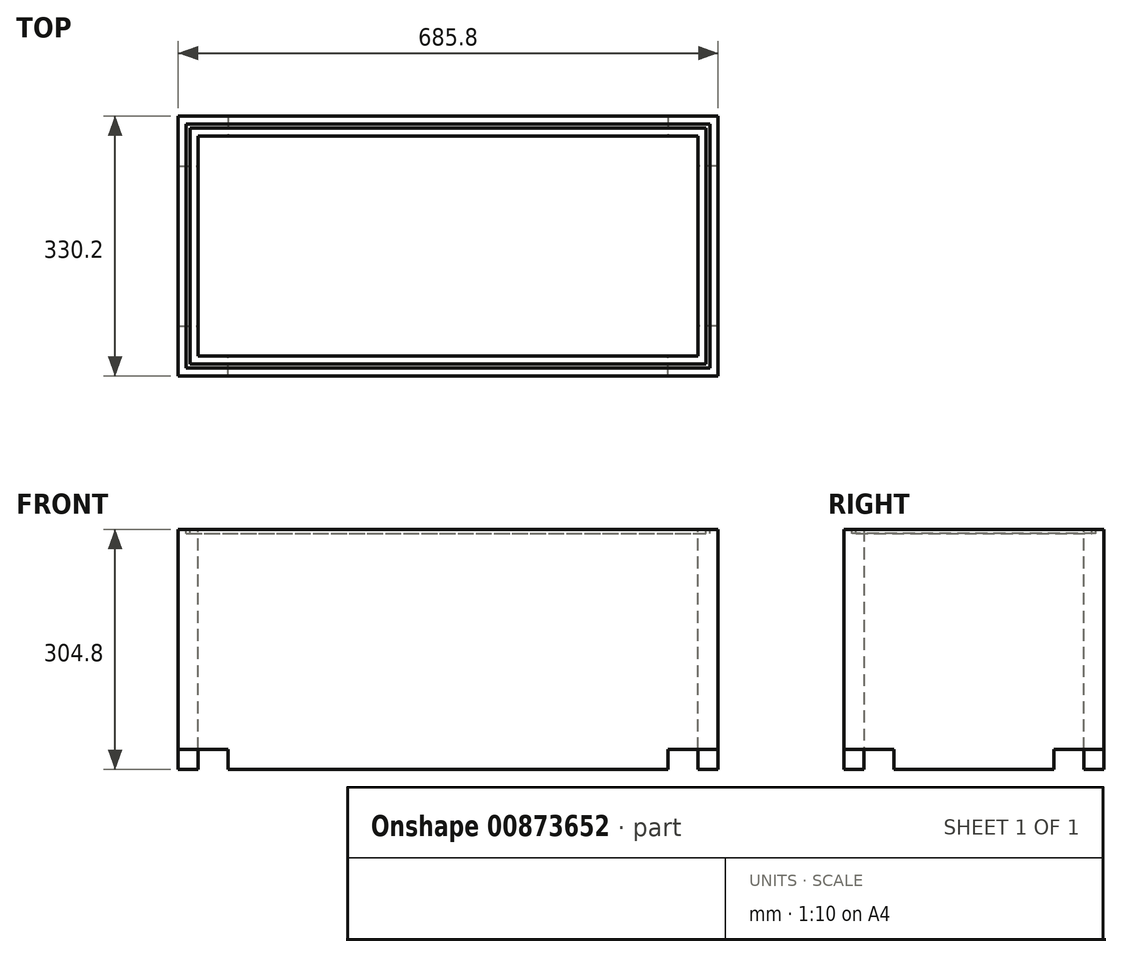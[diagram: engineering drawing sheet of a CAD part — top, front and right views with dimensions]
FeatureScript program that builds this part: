
annotation { "Feature Type Name" : "Feature", "Feature Type Description" : "" }
export const myFeature = defineFeature(function(context is Context, id is Id, definition is map)
    precondition{}
    {
        {
            var Q0;
            Q0=qCreatedBy(makeId("Top.planeOp"),FACE);
            var sketch = newSketch(context, id + "F0", { "sketchPlane" : qUnion([Q0])});
            skLineSegment(sketch, "E0.bottom", {"start": v(0, 0) * mm, "end": v(685.8, 0) * mm});
            skLineSegment(sketch, "E0.top", {"start": v(0, -25.4) * mm, "end": v(685.8, -25.4) * mm});
            skLineSegment(sketch, "E0.left", {"start": v(0, 0) * mm, "end": v(0, -25.4) * mm});
            skLineSegment(sketch, "E0.right", {"start": v(685.8, 0) * mm, "end": v(685.8, -25.4) * mm});
            skSolve(sketch);
        }
        {
            var Q0;
            Q0 = qSketchRegion(id + "F0", true);
            extrude(context, id + "F1", {"entities" : qUnion([Q0]), "depth" : 304.8 * mm, "offsetDistance" : 25.4 * mm});
        }
        {
            var Q0;
            Q0=makeQuery(id+"F1.opExtrude","SWEPT_FACE",FACE,{"disambiguationData":[OSD([sQuery(id+"F0.wireOp",EDGE,"E0.top")])]});
            var sketch = newSketch(context, id + "F2", { "sketchPlane" : qUnion([Q0])});
            skLineSegment(sketch, "E1.bottom", {"start": v(685.8, 0) * mm, "end": v(660.4, 0) * mm});
            skLineSegment(sketch, "E1.top", {"start": v(685.8, 304.8) * mm, "end": v(660.4, 304.8) * mm});
            skLineSegment(sketch, "E1.left", {"start": v(685.8, 0) * mm, "end": v(685.8, 304.8) * mm});
            skLineSegment(sketch, "E1.right", {"start": v(660.4, 0) * mm, "end": v(660.4, 304.8) * mm});
            skLineSegment(sketch, "E2.bottom", {"start": v(0, 0) * mm, "end": v(25.4, 0) * mm});
            skLineSegment(sketch, "E2.top", {"start": v(0, 304.8) * mm, "end": v(25.4, 304.8) * mm});
            skLineSegment(sketch, "E2.left", {"start": v(0, 0) * mm, "end": v(0, 304.8) * mm});
            skLineSegment(sketch, "E2.right", {"start": v(25.4, 0) * mm, "end": v(25.4, 304.8) * mm});
            skSolve(sketch);
        }
        {
            var Q0;
            Q0=makeQuery(id+"F2.imprint","IMPRINT",FACE,{"disambiguationData":[TD([[makeQuery(id+"F2.imprint","IMPRINT",EDGE,{"derivedFrom":sQuery(id+"F2.wireOp",EDGE,"E1.bottom")}),1.0]])]});
            extrude(context, id + "F3", {"entities" : qUnion([Q0]), "operationType" : NewBodyOperationType.ADD, "depth" : 304.8 * mm, "offsetDistance" : 25.4 * mm});
        }
        {
            var Q0;
            Q0=makeQuery(id+"F2.imprint","IMPRINT",FACE,{"disambiguationData":[TD([[makeQuery(id+"F2.imprint","IMPRINT",EDGE,{"derivedFrom":sQuery(id+"F2.wireOp",EDGE,"E2.bottom")}),1.0]])]});
            extrude(context, id + "F4", {"entities" : qUnion([Q0]), "operationType" : NewBodyOperationType.ADD, "depth" : 304.8 * mm, "offsetDistance" : 25.4 * mm});
        }
        {
            var Q0;
            Q0=makeQuery(id+"F4.opExtrude","SWEPT_FACE",FACE,{"disambiguationData":[OSD([sQuery(id+"F2.wireOp",EDGE,"E2.right")])]});
            var sketch = newSketch(context, id + "F5", { "sketchPlane" : qUnion([Q0])});
            skLineSegment(sketch, "E3.bottom", {"start": v(-330.2, 304.8) * mm, "end": v(-304.8, 304.8) * mm});
            skLineSegment(sketch, "E3.top", {"start": v(-330.2, 0) * mm, "end": v(-304.8, 0) * mm});
            skLineSegment(sketch, "E3.left", {"start": v(-330.2, 304.8) * mm, "end": v(-330.2, 0) * mm});
            skLineSegment(sketch, "E3.right", {"start": v(-304.8, 304.8) * mm, "end": v(-304.8, 0) * mm});
            skSolve(sketch);
        }
        {
            var Q0;
            Q0=makeQuery(id+"F5.imprint","IMPRINT",FACE,{"disambiguationData":[TD([[makeQuery(id+"F5.imprint","IMPRINT",EDGE,{"derivedFrom":sQuery(id+"F5.wireOp",EDGE,"E3.bottom")}),-1.0]])]});
            extrude(context, id + "F6", {"entities" : qUnion([Q0]), "operationType" : NewBodyOperationType.ADD, "depth" : 660.4 * mm, "offsetDistance" : 25.4 * mm});
        }
        {
            var Q0;
            Q0=makeQuery(id+"F6.boolean.opBoolean","MERGE",FACE,{"derivedFrom":[makeQuery(id+"F4.boolean.opBoolean","MERGE",FACE,{"derivedFrom":[makeQuery(id+"F3.boolean.opBoolean","MERGE",FACE,{"derivedFrom":[makeQuery(id+"F1.opExtrude","CAP_FACE",FACE,{"disambiguationData":[OSD([sQuery(id+"F0.wireOp",EDGE,"E0.bottom"),sQuery(id+"F0.wireOp",EDGE,"E0.top"),sQuery(id+"F0.wireOp",EDGE,"E0.left"),sQuery(id+"F0.wireOp",EDGE,"E0.right")])],"isStart":false}),makeQuery(id+"F3.opExtrude","SWEPT_FACE",FACE,{"disambiguationData":[OSD([sQuery(id+"F2.wireOp",EDGE,"E1.top")])]})]}),makeQuery(id+"F4.opExtrude","SWEPT_FACE",FACE,{"disambiguationData":[OSD([sQuery(id+"F2.wireOp",EDGE,"E2.top")])]})]}),makeQuery(id+"F6.opExtrude","SWEPT_FACE",FACE,{"disambiguationData":[OSD([sQuery(id+"F5.wireOp",EDGE,"E3.bottom")])]})]});
            var sketch = newSketch(context, id + "F7", { "sketchPlane" : qUnion([Q0])});
            skLineSegment(sketch, "E4.bottom", {"start": v(12.7, -10.16) * mm, "end": v(673.1, -10.16) * mm});
            skLineSegment(sketch, "E4.top", {"start": v(15.24, -15.24) * mm, "end": v(673.1, -15.24) * mm});
            skLineSegment(sketch, "E4.right", {"start": v(673.1, -10.16) * mm, "end": v(673.1, -15.24) * mm});
            skLineSegment(sketch, "E5.bottom", {"start": v(10.16, -10.16) * mm, "end": v(15.24, -10.16) * mm});
            skLineSegment(sketch, "E5.top", {"start": v(10.16, -314.96) * mm, "end": v(15.24, -314.96) * mm});
            skLineSegment(sketch, "E5.left", {"start": v(10.16, -10.16) * mm, "end": v(10.16, -314.96) * mm});
            skLineSegment(sketch, "E5.right", {"start": v(15.24, -10.16) * mm, "end": v(15.24, -314.96) * mm});
            skLineSegment(sketch, "E6.top", {"start": v(10.16, -15.24) * mm, "end": v(15.24, -15.24) * mm});
            skLineSegment(sketch, "E6.left", {"start": v(10.16, -10.16) * mm, "end": v(10.16, -15.24) * mm});
            skLineSegment(sketch, "E6.right", {"start": v(15.24, -10.16) * mm, "end": v(15.24, -15.24) * mm});
            skLineSegment(sketch, "E7.top", {"start": v(10.16, -320.04) * mm, "end": v(15.24, -320.04) * mm});
            skLineSegment(sketch, "E7.left", {"start": v(10.16, -314.96) * mm, "end": v(10.16, -320.04) * mm});
            skLineSegment(sketch, "E7.right", {"start": v(15.24, -314.96) * mm, "end": v(15.24, -320.04) * mm});
            skLineSegment(sketch, "E8.bottom", {"start": v(15.24, -314.96) * mm, "end": v(670.56, -314.96) * mm});
            skLineSegment(sketch, "E8.top", {"start": v(15.24, -320.04) * mm, "end": v(670.56, -320.04) * mm});
            skLineSegment(sketch, "E8.right", {"start": v(670.56, -314.96) * mm, "end": v(670.56, -320.04) * mm});
            skLineSegment(sketch, "E9.bottom", {"start": v(670.56, -314.96) * mm, "end": v(675.64, -314.96) * mm});
            skLineSegment(sketch, "E9.top", {"start": v(670.56, -320.04) * mm, "end": v(675.64, -320.04) * mm});
            skLineSegment(sketch, "E9.right", {"start": v(675.64, -314.96) * mm, "end": v(675.64, -320.04) * mm});
            skLineSegment(sketch, "E10.top", {"start": v(670.56, -10.16) * mm, "end": v(675.64, -10.16) * mm});
            skLineSegment(sketch, "E10.left", {"start": v(670.56, -314.96) * mm, "end": v(670.56, -10.16) * mm});
            skLineSegment(sketch, "E10.right", {"start": v(675.64, -314.96) * mm, "end": v(675.64, -10.16) * mm});
            skSolve(sketch);
        }
        {
            var Q0;
            {var subQ0=sQuery(id+"F7.wireOp",EDGE,"E4.bottom");Q0=makeQuery(id+"F7.imprint","IMPRINT",FACE,{"disambiguationData":[TD([[makeQuery(id+"F7.imprint","IMPRINT",EDGE,{"derivedFrom":subQ0}),-1.0]])]});}
            var Q1;
            Q1=makeQuery(id+"F7.imprint","IMPRINT",FACE,{"disambiguationData":[TD([[makeQuery(id+"F7.imprint","IMPRINT",EDGE,{"derivedFrom":sQuery(id+"F7.wireOp",EDGE,"E6.top")}),1.0]])]});
            var Q2;
            Q2=makeQuery(id+"F7.imprint","IMPRINT",FACE,{"disambiguationData":[TD([[makeQuery(id+"F7.imprint","IMPRINT",EDGE,{"derivedFrom":sQuery(id+"F7.wireOp",EDGE,"E5.left")}),1.0]])]});
            var Q3;
            Q3=makeQuery(id+"F7.imprint","IMPRINT",FACE,{"disambiguationData":[TD([[makeQuery(id+"F7.imprint","IMPRINT",EDGE,{"derivedFrom":sQuery(id+"F7.wireOp",EDGE,"E5.top")}),-1.0]])]});
            var Q4;
            Q4=makeQuery(id+"F7.imprint","IMPRINT",FACE,{"disambiguationData":[TD([[makeQuery(id+"F7.imprint","IMPRINT",EDGE,{"derivedFrom":sQuery(id+"F7.wireOp",EDGE,"E8.bottom")}),-1.0]])]});
            var Q5;
            Q5=makeQuery(id+"F7.imprint","IMPRINT",FACE,{"disambiguationData":[TD([[makeQuery(id+"F7.imprint","IMPRINT",EDGE,{"derivedFrom":sQuery(id+"F7.wireOp",EDGE,"E9.top")}),1.0]])]});
            var Q6;
            {var subQ1=sQuery(id+"F7.wireOp",EDGE,"E4.right");Q6=makeQuery(id+"F7.imprint","IMPRINT",FACE,{"disambiguationData":[TD([[makeQuery(id+"F7.imprint","IMPRINT",EDGE,{"derivedFrom":subQ1}),1.0]])]});}
            var Q7;
            {var subQ0=sQuery(id+"F7.wireOp",EDGE,"E4.right");Q7=makeQuery(id+"F7.imprint","IMPRINT",FACE,{"disambiguationData":[TD([[makeQuery(id+"F7.imprint","IMPRINT",EDGE,{"derivedFrom":subQ0}),-1.0]])]});}
            extrude(context, id + "F8", {"entities" : qUnion([Q0, Q1, Q2, Q3, Q4, Q5, Q6, Q7]), "operationType" : NewBodyOperationType.REMOVE, "oppositeDirection" : true, "depth" : 5.08 * mm, "offsetDistance" : 25.4 * mm});
        }
        {
            var Q0;
            Q0=makeQuery(id+"F6.boolean.opBoolean","MERGE",FACE,{"derivedFrom":[makeQuery(id+"F4.boolean.opBoolean","MERGE",FACE,{"derivedFrom":[makeQuery(id+"F3.boolean.opBoolean","MERGE",FACE,{"derivedFrom":[makeQuery(id+"F1.opExtrude","CAP_FACE",FACE,{"disambiguationData":[OSD([sQuery(id+"F0.wireOp",EDGE,"E0.bottom"),sQuery(id+"F0.wireOp",EDGE,"E0.top"),sQuery(id+"F0.wireOp",EDGE,"E0.left"),sQuery(id+"F0.wireOp",EDGE,"E0.right")])],"isStart":true}),makeQuery(id+"F3.opExtrude","SWEPT_FACE",FACE,{"disambiguationData":[OSD([sQuery(id+"F2.wireOp",EDGE,"E1.bottom")])]})]}),makeQuery(id+"F4.opExtrude","SWEPT_FACE",FACE,{"disambiguationData":[OSD([sQuery(id+"F2.wireOp",EDGE,"E2.bottom")])]})]}),makeQuery(id+"F6.opExtrude","SWEPT_FACE",FACE,{"disambiguationData":[OSD([sQuery(id+"F5.wireOp",EDGE,"E3.top")])]})]});
            var sketch = newSketch(context, id + "F9", { "sketchPlane" : qUnion([Q0])});
            skLineSegment(sketch, "E11.bottom", {"start": v(685.8, 0) * mm, "end": v(622.3, 0) * mm});
            skLineSegment(sketch, "E11.top", {"start": v(685.8, 63.5) * mm, "end": v(622.3, 63.5) * mm});
            skLineSegment(sketch, "E11.left", {"start": v(685.8, 0) * mm, "end": v(685.8, 63.5) * mm});
            skLineSegment(sketch, "E11.right", {"start": v(622.3, 0) * mm, "end": v(622.3, 63.5) * mm});
            skLineSegment(sketch, "E12.bottom", {"start": v(685.8, 330.2) * mm, "end": v(622.3, 330.2) * mm});
            skLineSegment(sketch, "E12.top", {"start": v(685.8, 266.7) * mm, "end": v(622.3, 266.7) * mm});
            skLineSegment(sketch, "E12.left", {"start": v(685.8, 330.2) * mm, "end": v(685.8, 266.7) * mm});
            skLineSegment(sketch, "E12.right", {"start": v(622.3, 330.2) * mm, "end": v(622.3, 266.7) * mm});
            skLineSegment(sketch, "E13.bottom", {"start": v(0, 330.2) * mm, "end": v(63.5, 330.2) * mm});
            skLineSegment(sketch, "E13.top", {"start": v(0, 266.7) * mm, "end": v(63.5, 266.7) * mm});
            skLineSegment(sketch, "E13.left", {"start": v(0, 330.2) * mm, "end": v(0, 266.7) * mm});
            skLineSegment(sketch, "E13.right", {"start": v(63.5, 330.2) * mm, "end": v(63.5, 266.7) * mm});
            skLineSegment(sketch, "E14.bottom", {"start": v(0, 0) * mm, "end": v(63.5, 0) * mm});
            skLineSegment(sketch, "E14.top", {"start": v(0, 63.5) * mm, "end": v(63.5, 63.5) * mm});
            skLineSegment(sketch, "E14.left", {"start": v(0, 0) * mm, "end": v(0, 63.5) * mm});
            skLineSegment(sketch, "E14.right", {"start": v(63.5, 0) * mm, "end": v(63.5, 63.5) * mm});
            skSolve(sketch);
        }
        {
            var Q0;
            Q0 = qSketchRegion(id + "F9", true);
            extrude(context, id + "F10", {"entities" : qUnion([Q0]), "operationType" : NewBodyOperationType.REMOVE, "oppositeDirection" : true, "depth" : 25.4 * mm, "offsetDistance" : 25.4 * mm});
        }
    });
